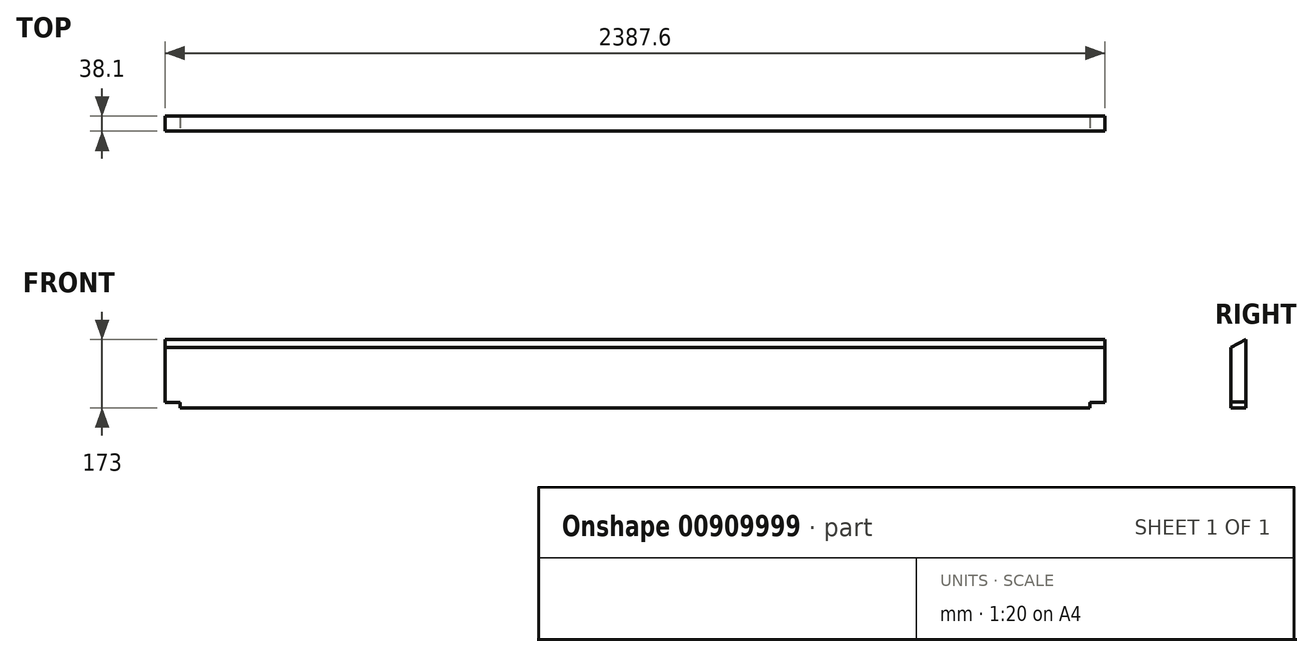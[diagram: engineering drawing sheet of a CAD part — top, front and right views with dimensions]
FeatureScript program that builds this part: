
annotation { "Feature Type Name" : "Feature", "Feature Type Description" : "" }
export const myFeature = defineFeature(function(context is Context, id is Id, definition is map)
    precondition{}
    {
        {
            var Q0;
            Q0=qCreatedBy(makeId("Right.planeOp"),FACE);
            var sketch = newSketch(context, id + "F0", { "sketchPlane" : qUnion([Q0])});
            skLineSegment(sketch, "E0.bottom", {"start": v(19.05, 1331.91) * mm, "end": v(-19.05, 1331.91) * mm});
            skLineSegment(sketch, "E0.top", {"start": v(19.05, 1504.91) * mm, "end": v(-19.05, 1485.5) * mm});
            skLineSegment(sketch, "E0.left", {"start": v(19.05, 1331.91) * mm, "end": v(19.05, 1504.91) * mm});
            skLineSegment(sketch, "E0.right", {"start": v(-19.05, 1331.91) * mm, "end": v(-19.05, 1346.07) * mm});
            skLineSegment(sketch, "E1", {"start": v(0, 1331.91) * mm, "end": v(0, 0) * mm, "construction": true});
            skLineSegment(sketch, "E2", {"start": v(19.05, 1346.07) * mm, "end": v(19.05, 1346.07) * mm});
            skLineSegment(sketch, "E3", {"start": v(-19.05, 1346.07) * mm, "end": v(-19.05, 1485.5) * mm});
            skArc(sketch, "E4", {"start": v(19.05, 1346.07) * mm, "mid": v(0, 1346.2) * mm, "end": v(-19.05, 1346.07) * mm});
            skLineSegment(sketch, "E5", {"start": v(0, 1331.91) * mm, "end": v(0, 1346.2) * mm, "construction": true});
            skSolve(sketch);
        }
        {
            var Q0;
            {var subQ0=sQuery(id+"F0.wireOp",EDGE,"E0.top");Q0=makeQuery(id+"F0.imprint","IMPRINT",FACE,{"disambiguationData":[TD([[makeQuery(id+"F0.imprint","IMPRINT",EDGE,{"derivedFrom":subQ0}),1.0]])]});}
            extrude(context, id + "F1", {"entities" : qUnion([Q0]), "flatOperationType" : FlatOperationType.REMOVE, "depth" : 2387.6 * mm, "offsetDistance" : 25 * mm, "domain" : OperationDomain.MODEL, "symmetric" : true});
        }
        {
            var Q0;
            {var subQ0=sQuery(id+"F0.wireOp",EDGE,"E0.bottom");Q0=makeQuery(id+"F0.imprint","IMPRINT",FACE,{"disambiguationData":[TD([[makeQuery(id+"F0.imprint","IMPRINT",EDGE,{"derivedFrom":subQ0}),-1.0]])]});}
            extrude(context, id + "F2", {"entities" : qUnion([Q0]), "operationType" : NewBodyOperationType.ADD, "flatOperationType" : FlatOperationType.REMOVE, "depth" : 2311.4 * mm, "offsetDistance" : 25 * mm, "domain" : OperationDomain.MODEL, "symmetric" : true});
        }
    });
